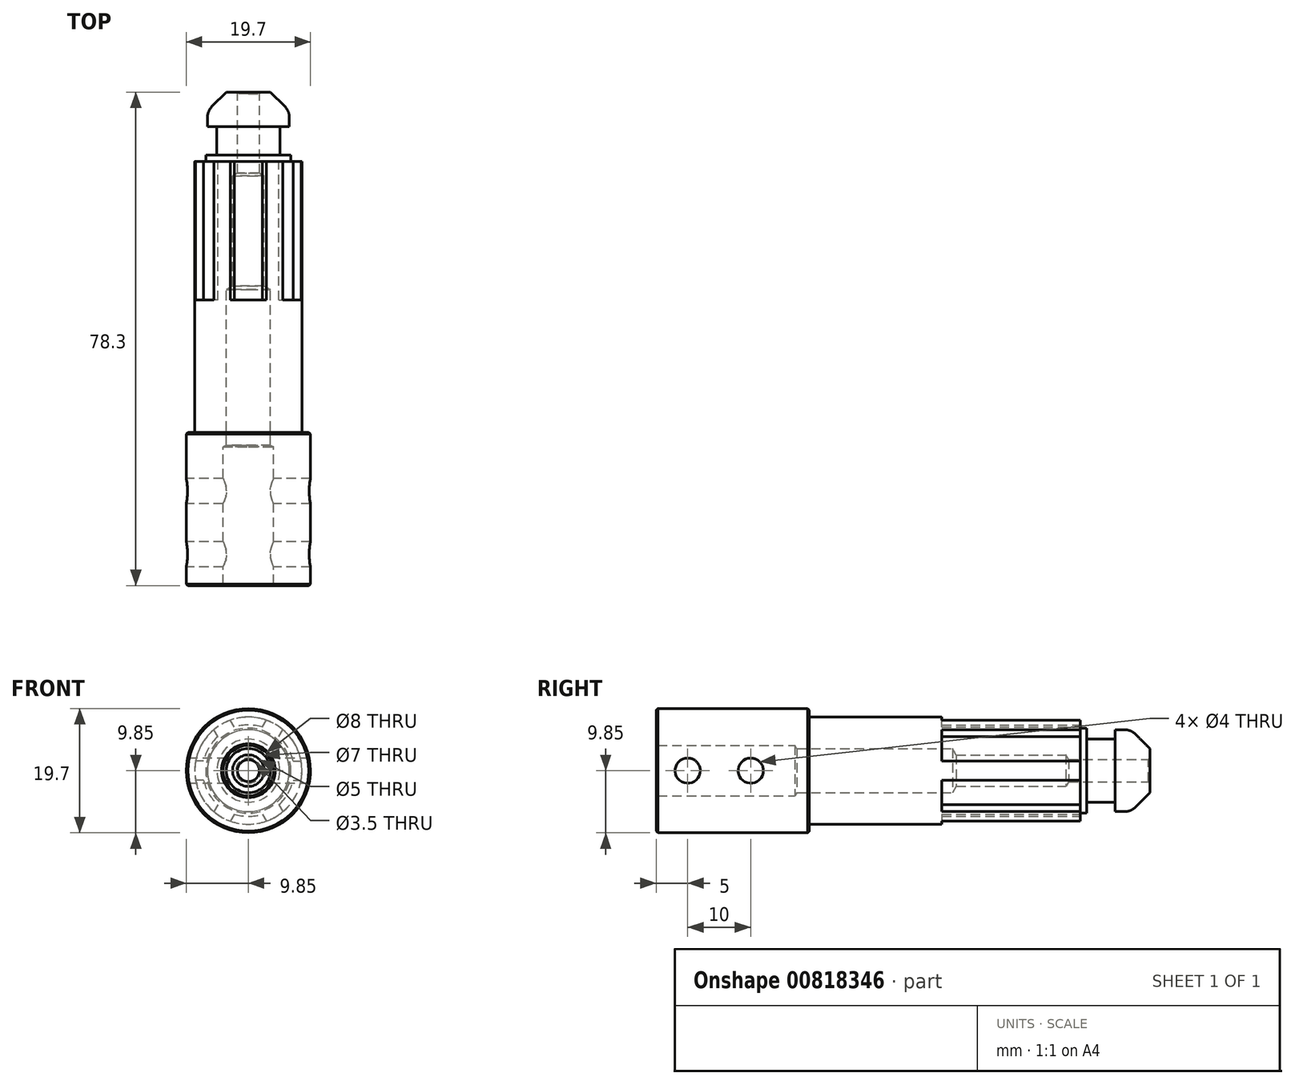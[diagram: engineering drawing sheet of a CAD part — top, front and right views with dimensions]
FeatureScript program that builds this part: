
annotation { "Feature Type Name" : "Feature", "Feature Type Description" : "" }
export const myFeature = defineFeature(function(context is Context, id is Id, definition is map)
    precondition{}
    {
        {
            var Q0;
            Q0=qCreatedBy(makeId("Right.planeOp"),FACE);
            var sketch = newSketch(context, id + "F0", { "sketchPlane" : qUnion([Q0])});
            skLineSegment(sketch, "E0", {"start": v(0, 0) * mm, "end": v(0, 9.85) * mm});
            skLineSegment(sketch, "E1", {"start": v(0, 9.85) * mm, "end": v(24.3, 9.85) * mm});
            skLineSegment(sketch, "E2", {"start": v(24.3, 9.85) * mm, "end": v(24.3, 8.5) * mm});
            skLineSegment(sketch, "E3", {"start": v(24.3, 8.5) * mm, "end": v(67.3, 8.5) * mm});
            skLineSegment(sketch, "E4", {"start": v(67.3, 8.5) * mm, "end": v(67.3, 6.75) * mm});
            skLineSegment(sketch, "E5", {"start": v(67.3, 6.75) * mm, "end": v(68.3, 6.75) * mm});
            skLineSegment(sketch, "E6", {"start": v(68.3, 6.75) * mm, "end": v(68.3, 5) * mm});
            skLineSegment(sketch, "E7", {"start": v(68.3, 5) * mm, "end": v(72.8, 5) * mm});
            skLineSegment(sketch, "E8", {"start": v(72.8, 5) * mm, "end": v(72.8, 6.5) * mm});
            skLineSegment(sketch, "E9", {"start": v(72.8, 6.5) * mm, "end": v(75.3, 6.5) * mm});
            skLineSegment(sketch, "E10", {"start": v(75.3, 6.5) * mm, "end": v(78.3, 3.5) * mm});
            skLineSegment(sketch, "E11", {"start": v(78.3, 3.5) * mm, "end": v(78.3, 0) * mm});
            skLineSegment(sketch, "E12", {"start": v(78.3, 0) * mm, "end": v(0, 0) * mm});
            skLineSegment(sketch, "E13", {"start": v(0, 4) * mm, "end": v(22, 4) * mm});
            skLineSegment(sketch, "E14", {"start": v(22.29, 3.5) * mm, "end": v(47, 3.5) * mm});
            skLineSegment(sketch, "E15", {"start": v(47.58, 2.5) * mm, "end": v(65, 2.5) * mm});
            skLineSegment(sketch, "E16", {"start": v(65.43, 1.75) * mm, "end": v(78.3, 1.75) * mm});
            skLineSegment(sketch, "E17", {"start": v(22, 4) * mm, "end": v(22.29, 3.5) * mm});
            skLineSegment(sketch, "E18", {"start": v(47, 3.5) * mm, "end": v(47.58, 2.5) * mm});
            skLineSegment(sketch, "E19", {"start": v(65, 2.5) * mm, "end": v(65.43, 1.75) * mm});
            skSolve(sketch);
        }
        {
            var Q0;
            {var subQ0=sQuery(id+"F0.wireOp",EDGE,"E1");Q0=makeQuery(id+"F0.imprint","IMPRINT",FACE,{"disambiguationData":[TD([[makeQuery(id+"F0.imprint","IMPRINT",EDGE,{"derivedFrom":subQ0}),-1.0]])]});}
            var Q1;
            Q1=sQuery(id+"F0.wireOp",EDGE,"E12");
            revolve(context, id + "F1", {"surfaceOperationType" : NewSurfaceOperationType.NEW, "entities" : qUnion([Q0]), "axis" : qUnion([Q1]), "revolveType" : RevolveType.FULL});
        }
        {
            var Q0;
            Q0=makeQuery(id+"F1.opRevolve","SWEPT_FACE",FACE,{"disambiguationData":[OSD([sQuery(id+"F0.wireOp",EDGE,"E4")])]});
            var sketch = newSketch(context, id + "F2", { "sketchPlane" : qUnion([Q0])});
            skLineSegment(sketch, "E20", {"start": v(0, 0) * mm, "end": v(11.9, 0) * mm, "construction": true});
            skLineSegment(sketch, "E21.0", {"start": v(7.1, 1.5) * mm, "end": v(8.87, 1.5) * mm});
            skLineSegment(sketch, "E22.0", {"start": v(7.1, -1.5) * mm, "end": v(8.87, -1.5) * mm});
            skCircle(sketch, "E23", {"center": v(0, 0) * mm, "radius": 7.25 * mm});
            skCircle(sketch, "E24", {"center": v(0, 0) * mm, "radius": 9 * mm});
            skLineSegment(sketch, "E25.1.0", {"start": v(2.25, 6.9) * mm, "end": v(3.14, 8.44) * mm});
            skLineSegment(sketch, "E25.1.1", {"start": v(4.85, 5.4) * mm, "end": v(5.74, 6.94) * mm});
            skLineSegment(sketch, "E25.2.0", {"start": v(-4.85, 5.4) * mm, "end": v(-5.74, 6.94) * mm});
            skLineSegment(sketch, "E25.2.1", {"start": v(-2.25, 6.9) * mm, "end": v(-3.14, 8.44) * mm});
            skLineSegment(sketch, "E25.3.0", {"start": v(-7.1, -1.5) * mm, "end": v(-8.87, -1.5) * mm});
            skLineSegment(sketch, "E25.3.1", {"start": v(-7.1, 1.5) * mm, "end": v(-8.87, 1.5) * mm});
            skLineSegment(sketch, "E25.4.0", {"start": v(-2.25, -6.9) * mm, "end": v(-3.14, -8.44) * mm});
            skLineSegment(sketch, "E25.4.1", {"start": v(-4.85, -5.4) * mm, "end": v(-5.74, -6.94) * mm});
            skLineSegment(sketch, "E25.5.0", {"start": v(4.85, -5.4) * mm, "end": v(5.74, -6.94) * mm});
            skLineSegment(sketch, "E25.5.1", {"start": v(2.25, -6.9) * mm, "end": v(3.14, -8.44) * mm});
            skSolve(sketch);
        }
        {
            var Q0;
            {var subQ0=sQuery(id+"F2.wireOp",EDGE,"E25.2.0");var subQ1=sQuery(id+"F2.wireOp",EDGE,"E23");var subQ2=makeQuery(id+"F2.imprint","INTERSECT",VERTEX,{"derivedFrom":[subQ1,subQ0]});Q0=makeQuery(id+"F2.imprint","IMPRINT",FACE,{"disambiguationData":[TD([[makeQuery(id+"F2.imprint","IMPRINT",EDGE,{"disambiguationData":[TD([[subQ2,-1.0]])],"derivedFrom":subQ1}),-1.0]])]});}
            var Q1;
            {var subQ0=sQuery(id+"F2.wireOp",EDGE,"E25.3.0");var subQ1=sQuery(id+"F2.wireOp",EDGE,"E23");var subQ2=makeQuery(id+"F2.imprint","INTERSECT",VERTEX,{"derivedFrom":[subQ1,subQ0]});Q1=makeQuery(id+"F2.imprint","IMPRINT",FACE,{"disambiguationData":[TD([[makeQuery(id+"F2.imprint","IMPRINT",EDGE,{"disambiguationData":[TD([[subQ2,-1.0]])],"derivedFrom":subQ1}),-1.0]])]});}
            var Q2;
            {var subQ0=sQuery(id+"F2.wireOp",EDGE,"E25.1.0");var subQ1=sQuery(id+"F2.wireOp",EDGE,"E23");var subQ2=makeQuery(id+"F2.imprint","INTERSECT",VERTEX,{"derivedFrom":[subQ1,subQ0]});Q2=makeQuery(id+"F2.imprint","IMPRINT",FACE,{"disambiguationData":[TD([[makeQuery(id+"F2.imprint","IMPRINT",EDGE,{"disambiguationData":[TD([[subQ2,-1.0]])],"derivedFrom":subQ1}),-1.0]])]});}
            var Q3;
            {var subQ0=sQuery(id+"F2.wireOp",EDGE,"E23");var subQ1=sQuery(id+"F2.wireOp",EDGE,"E21.0");var subQ2=makeQuery(id+"F2.imprint","INTERSECT",VERTEX,{"derivedFrom":[subQ1,subQ0]});Q3=makeQuery(id+"F2.imprint","IMPRINT",FACE,{"disambiguationData":[TD([[makeQuery(id+"F2.imprint","IMPRINT",EDGE,{"disambiguationData":[TD([[subQ2,-1.0]])],"derivedFrom":subQ0}),-1.0]])]});}
            var Q4;
            {var subQ0=sQuery(id+"F2.wireOp",EDGE,"E23");var subQ1=sQuery(id+"F2.wireOp",EDGE,"E22.0");var subQ2=makeQuery(id+"F2.imprint","INTERSECT",VERTEX,{"derivedFrom":[subQ1,subQ0]});Q4=makeQuery(id+"F2.imprint","IMPRINT",FACE,{"disambiguationData":[TD([[makeQuery(id+"F2.imprint","IMPRINT",EDGE,{"disambiguationData":[TD([[subQ2,1.0]])],"derivedFrom":subQ0}),-1.0]])]});}
            var Q5;
            {var subQ0=sQuery(id+"F2.wireOp",EDGE,"E25.4.0");var subQ1=sQuery(id+"F2.wireOp",EDGE,"E23");var subQ2=makeQuery(id+"F2.imprint","INTERSECT",VERTEX,{"derivedFrom":[subQ1,subQ0]});Q5=makeQuery(id+"F2.imprint","IMPRINT",FACE,{"disambiguationData":[TD([[makeQuery(id+"F2.imprint","IMPRINT",EDGE,{"disambiguationData":[TD([[subQ2,-1.0]])],"derivedFrom":subQ1}),-1.0]])]});}
            extrude(context, id + "F3", {"entities" : qUnion([Q0, Q1, Q2, Q3, Q4, Q5]), "operationType" : NewBodyOperationType.REMOVE, "oppositeDirection" : true, "depth" : 22 * mm, "offsetDistance" : 25 * mm});
        }
        {
            var Q0;
            Q0=qCreatedBy(makeId("Right.planeOp"),FACE);
            cPlane(context, id + "F4", {"entities" : qUnion([Q0]), "cplaneType" : CPlaneType.OFFSET, "offset" : 12 * mm, "width" : 150 * mm, "height" : 150 * mm});
        }
        {
            var Q0;
            Q0=qCreatedBy(id+"F4.planeOp",FACE);
            var sketch = newSketch(context, id + "F5", { "sketchPlane" : qUnion([Q0])});
            skPoint(sketch, "E26", {"position": v(5, 0) * mm});
            skPoint(sketch, "E27", {"position": v(15, 0) * mm});
            skSolve(sketch);
        }
        {
            var Q0;
            Q0=sQuery(id+"F5.wireOp",VERTEX,"E26");
            var Q1;
            Q1=sQuery(id+"F5.wireOp",VERTEX,"E27");
            var Q2;
            Q2=makeQuery(id+"F1.opRevolve","SWEPT_BODY",BODY,{"disambiguationData":[OSD([sQuery(id+"F0.wireOp",EDGE,"E0"),sQuery(id+"F0.wireOp",EDGE,"E1"),sQuery(id+"F0.wireOp",EDGE,"E2"),sQuery(id+"F0.wireOp",EDGE,"E3"),sQuery(id+"F0.wireOp",EDGE,"E4"),sQuery(id+"F0.wireOp",EDGE,"E5"),sQuery(id+"F0.wireOp",EDGE,"E6"),sQuery(id+"F0.wireOp",EDGE,"E7"),sQuery(id+"F0.wireOp",EDGE,"E8"),sQuery(id+"F0.wireOp",EDGE,"E9"),sQuery(id+"F0.wireOp",EDGE,"E10"),sQuery(id+"F0.wireOp",EDGE,"E11"),sQuery(id+"F0.wireOp",EDGE,"E13"),sQuery(id+"F0.wireOp",EDGE,"e68096d0-78ae-42cb-be89-78c10eaa8a64"),sQuery(id+"F0.wireOp",EDGE,"E14"),sQuery(id+"F0.wireOp",EDGE,"16d07636-ebb1-430f-b086-ed3c86e72aca"),sQuery(id+"F0.wireOp",EDGE,"E15"),sQuery(id+"F0.wireOp",EDGE,"0d4d28b8-dc0e-4f0c-a840-340cf4f9dd3d"),sQuery(id+"F0.wireOp",EDGE,"E16")])]});
            hole(context, id + "F6", {"style" : HoleStyle.SIMPLE, "endStyle" : HoleEndStyle.THROUGH, "holeDiameter" : 4 * mm, "majorDiameter" : 5 * mm, "isTappedThrough" : true, "tappedDepth" : 12 * mm, "tapClearance" : 3, "locations" : qUnion([Q0, Q1]), "scope" : qUnion([Q2])});
        }
        {
            var Q0;
            Q0=makeQuery(id+"F1.opRevolve","SWEPT_EDGE",EDGE,{"disambiguationData":[OSD([sQuery(id+"F0.wireOp",EDGE,"E1"),sQuery(id+"F0.wireOp",EDGE,"E2")])]});
            var Q1;
            Q1=makeQuery(id+"F6.hole-1.boolean.opBoolean","INTERSECT",EDGE,{"disambiguationData":[OD(1.0)],"derivedFrom":[makeQuery(id+"F1.opRevolve","SWEPT_FACE",FACE,{"disambiguationData":[OSD([sQuery(id+"F0.wireOp",EDGE,"E1")])]}),makeQuery(id+"F6.hole-1.opRevolve","SWEPT_FACE",FACE,{"disambiguationData":[OSD([sQuery(id+"F6.hole-1.sketch.wireOp",EDGE,"core_line_2")])]})]});
            var Q2;
            Q2=makeQuery(id+"F6.hole-0.boolean.opBoolean","INTERSECT",EDGE,{"disambiguationData":[OD(1.0)],"derivedFrom":[makeQuery(id+"F1.opRevolve","SWEPT_FACE",FACE,{"disambiguationData":[OSD([sQuery(id+"F0.wireOp",EDGE,"E1")])]}),makeQuery(id+"F6.hole-0.opRevolve","SWEPT_FACE",FACE,{"disambiguationData":[OSD([sQuery(id+"F6.hole-0.sketch.wireOp",EDGE,"core_line_2")])]})]});
            var Q3;
            Q3=makeQuery(id+"F6.hole-0.boolean.opBoolean","INTERSECT",EDGE,{"disambiguationData":[OD(0.0)],"derivedFrom":[makeQuery(id+"F1.opRevolve","SWEPT_FACE",FACE,{"disambiguationData":[OSD([sQuery(id+"F0.wireOp",EDGE,"E1")])]}),makeQuery(id+"F6.hole-0.opRevolve","SWEPT_FACE",FACE,{"disambiguationData":[OSD([sQuery(id+"F6.hole-0.sketch.wireOp",EDGE,"core_line_2")])]})]});
            var Q4;
            Q4=makeQuery(id+"F6.hole-1.boolean.opBoolean","INTERSECT",EDGE,{"disambiguationData":[OD(0.0)],"derivedFrom":[makeQuery(id+"F1.opRevolve","SWEPT_FACE",FACE,{"disambiguationData":[OSD([sQuery(id+"F0.wireOp",EDGE,"E1")])]}),makeQuery(id+"F6.hole-1.opRevolve","SWEPT_FACE",FACE,{"disambiguationData":[OSD([sQuery(id+"F6.hole-1.sketch.wireOp",EDGE,"core_line_2")])]})]});
            var Q5;
            Q5=makeQuery(id+"F1.opRevolve","SWEPT_EDGE",EDGE,{"disambiguationData":[OSD([sQuery(id+"F0.wireOp",EDGE,"E0"),sQuery(id+"F0.wireOp",EDGE,"E1")])]});
            var Q6;
            Q6=makeQuery(id+"F1.opRevolve","SWEPT_EDGE",EDGE,{"disambiguationData":[OSD([sQuery(id+"F0.wireOp",EDGE,"E11"),sQuery(id+"F0.wireOp",EDGE,"E16")])]});
            var Q7;
            Q7=makeQuery(id+"F1.opRevolve","SWEPT_EDGE",EDGE,{"disambiguationData":[OSD([sQuery(id+"F0.wireOp",EDGE,"E0"),sQuery(id+"F0.wireOp",EDGE,"E13")])]});
            chamfer(context, id + "F7", {"entities" : qUnion([Q0, Q1, Q2, Q3, Q4, Q5, Q6, Q7]), "width" : 0.25 * mm, "tangentPropagation" : true});
        }
        {
            var Q0;
            Q0=makeQuery(id+"F1.opRevolve","SWEPT_EDGE",EDGE,{"disambiguationData":[OSD([sQuery(id+"F0.wireOp",EDGE,"E9"),sQuery(id+"F0.wireOp",EDGE,"E10")])]});
            fillet(context, id + "F8", {"entities" : qUnion([Q0]), "radius" : 2.5 * mm, "tangentPropagation" : true, "allowEdgeOverflow" : false});
        }
    });
